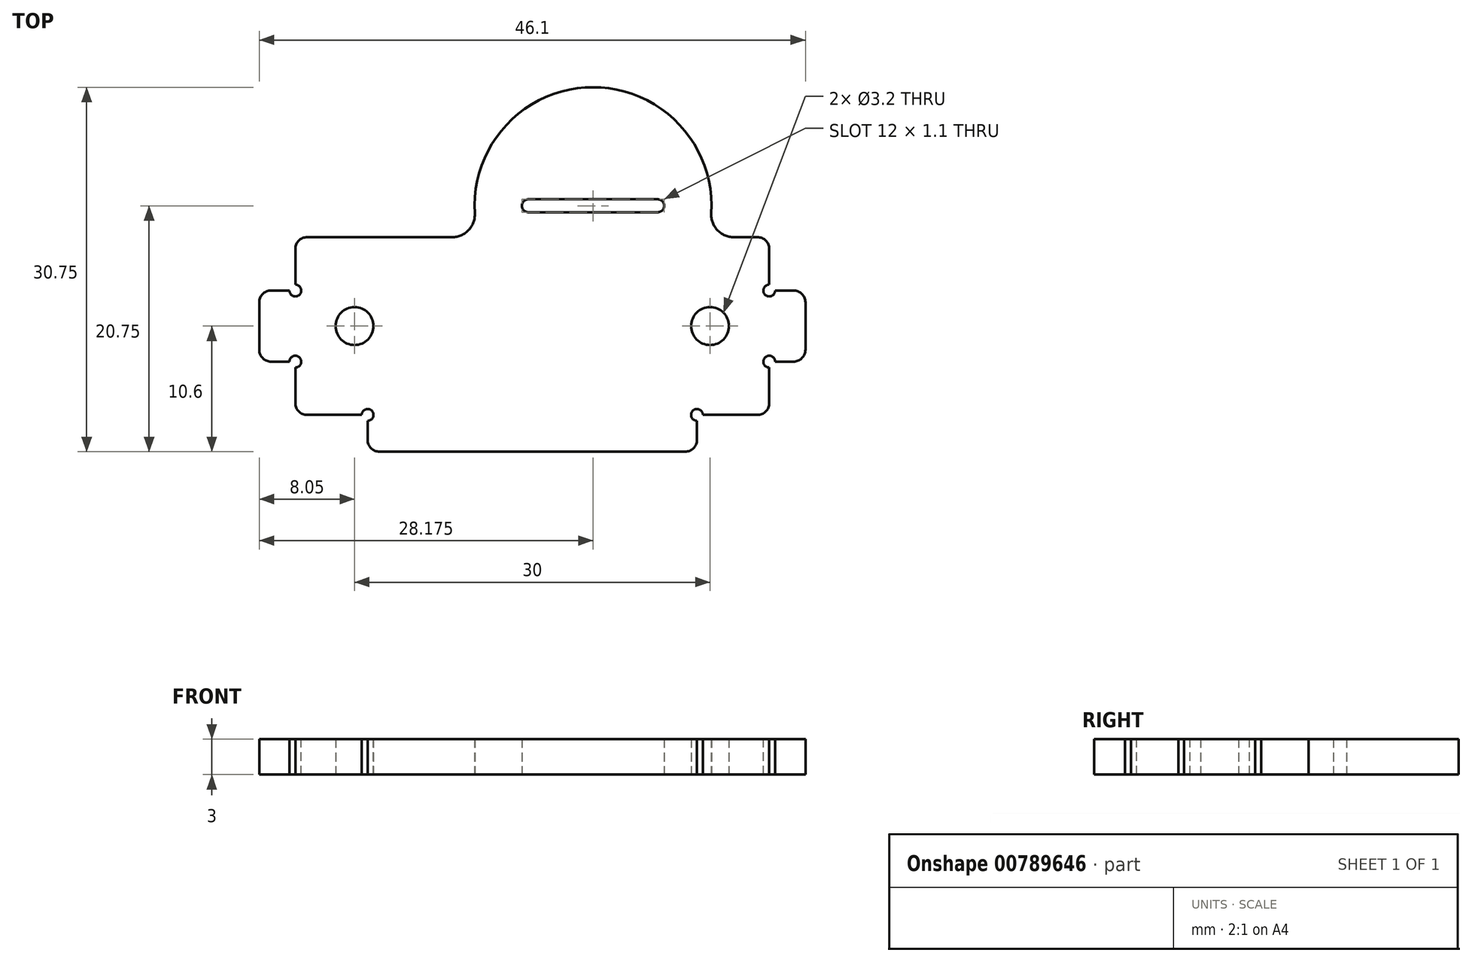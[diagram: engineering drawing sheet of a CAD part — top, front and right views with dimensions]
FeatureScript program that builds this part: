
annotation { "Feature Type Name" : "Feature", "Feature Type Description" : "" }
export const myFeature = defineFeature(function(context is Context, id is Id, definition is map)
    precondition{}
    {
        {
            var Q0;
            Q0=qCreatedBy(makeId("Top.planeOp"),FACE);
            var sketch = newSketch(context, id + "F0", { "sketchPlane" : qUnion([Q0])});
            skLineSegment(sketch, "E0", {"start": v(0, 0) * mm, "end": v(-20, 0) * mm, "construction": true});
            skLineSegment(sketch, "E1", {"start": v(0, 0) * mm, "end": v(0, 11.6) * mm, "construction": true});
            skLineSegment(sketch, "E2.MirrorCS", {"start": v(-20, -7.5) * mm, "end": v(-13.9, -7.5) * mm});
            skLineSegment(sketch, "E3.MirrorCS", {"start": v(-13.9, -10.6) * mm, "end": v(-13.9, -7.5) * mm});
            skLineSegment(sketch, "E4.MirrorCS", {"start": v(20, 7.5) * mm, "end": v(17, 7.5) * mm});
            skLineSegment(sketch, "E5.MirrorCS", {"start": v(20, -7.5) * mm, "end": v(13.9, -7.5) * mm});
            skLineSegment(sketch, "E6.MirrorCS", {"start": v(13.9, -10.6) * mm, "end": v(13.9, -7.5) * mm});
            skCircle(sketch, "E7", {"center": v(-15, 0) * mm, "radius": 1.6 * mm});
            skCircle(sketch, "E8.MirrorC", {"center": v(15, 0) * mm, "radius": 1.6 * mm});
            skCircle(sketch, "E9", {"center": v(5.13, 10.15) * mm, "radius": 6 * mm, "construction": true});
            skPoint(sketch, "E10.visualSharp", {"position": v(4.24, 7.5) * mm});
            skLineSegment(sketch, "E11", {"start": v(-20, 7.5) * mm, "end": v(-6.75, 7.5) * mm});
            skArc(sketch, "E12", {"start": v(15.1, 9.52) * mm, "mid": v(5.13, 20.15) * mm, "end": v(-4.86, 9.52) * mm});
            skPoint(sketch, "E13.visualSharp", {"position": v(-1.05, 7.5) * mm});
            skArc(sketch, "E13.filletArc", {"start": v(-6.75, 7.5) * mm, "mid": v(-5.37, 8.1) * mm, "end": v(-4.86, 9.52) * mm});
            skPoint(sketch, "E14.visualSharp", {"position": v(13.56, 7.5) * mm});
            skArc(sketch, "E14.filletArc", {"start": v(15.1, 9.52) * mm, "mid": v(15.62, 8.1) * mm, "end": v(17, 7.5) * mm});
            skLineSegment(sketch, "E15", {"start": v(-4.86, 9.52) * mm, "end": v(15.1, 9.52) * mm, "construction": true});
            skLineSegment(sketch, "E16.trimOffspring", {"start": v(-20, 7.5) * mm, "end": v(-20, 0) * mm});
            skLineSegment(sketch, "E17.trimOffspring", {"start": v(-20, -7.5) * mm, "end": v(-20, 0) * mm});
            skLineSegment(sketch, "E18.trimOffspring", {"start": v(20, -7.5) * mm, "end": v(20, 0) * mm});
            skLineSegment(sketch, "E19.trimOffspring", {"start": v(20, 7.5) * mm, "end": v(20, 0) * mm});
            skCircle(sketch, "E20", {"center": v(15, 0) * mm, "radius": 3 * mm, "construction": true});
            skCircle(sketch, "E21", {"center": v(-15, 0) * mm, "radius": 3 * mm, "construction": true});
            skLineSegment(sketch, "E22", {"start": v(-13.9, -10.6) * mm, "end": v(13.9, -10.6) * mm});
            skLineSegment(sketch, "E23.bottom", {"start": v(-0.32, 10.7) * mm, "end": v(10.58, 10.7) * mm});
            skLineSegment(sketch, "E23.top", {"start": v(-0.32, 9.6) * mm, "end": v(10.58, 9.6) * mm});
            skLineSegment(sketch, "E23.left", {"start": v(-0.32, 10.7) * mm, "end": v(-0.32, 9.6) * mm, "construction": true});
            skLineSegment(sketch, "E23.right", {"start": v(10.58, 10.7) * mm, "end": v(10.58, 9.6) * mm, "construction": true});
            skLineSegment(sketch, "E24", {"start": v(-0.32, 10.15) * mm, "end": v(10.58, 10.15) * mm, "construction": true});
            skCircle(sketch, "E25", {"center": v(-0.32, 10.15) * mm, "radius": 0.55 * mm});
            skCircle(sketch, "E26", {"center": v(10.58, 10.15) * mm, "radius": 0.55 * mm});
            skSolve(sketch);
        }
        {
            var Q0;
            Q0 = qSketchRegion(id + "F0", true);
            extrude(context, id + "F1", {"entities" : qUnion([Q0]), "depth" : 3 * mm, "offsetDistance" : 25 * mm});
        }
        {
            var Q0;
            Q0=makeQuery(id+"F1.opExtrude","CAP_FACE",FACE,{"disambiguationData":[OSD([sQuery(id+"F0.wireOp",EDGE,"E2.MirrorCS"),sQuery(id+"F0.wireOp",EDGE,"E3.MirrorCS"),sQuery(id+"F0.wireOp",EDGE,"E4.MirrorCS"),sQuery(id+"F0.wireOp",EDGE,"E5.MirrorCS"),sQuery(id+"F0.wireOp",EDGE,"E6.MirrorCS"),sQuery(id+"F0.wireOp",EDGE,"E7"),sQuery(id+"F0.wireOp",EDGE,"E8.MirrorC"),sQuery(id+"F0.wireOp",EDGE,"E9"),sQuery(id+"F0.wireOp",EDGE,"E11"),sQuery(id+"F0.wireOp",EDGE,"E12"),sQuery(id+"F0.wireOp",EDGE,"E13.filletArc"),sQuery(id+"F0.wireOp",EDGE,"E14.filletArc"),sQuery(id+"F0.wireOp",EDGE,"E16.trimOffspring"),sQuery(id+"F0.wireOp",EDGE,"E17.trimOffspring"),sQuery(id+"F0.wireOp",EDGE,"E18.trimOffspring"),sQuery(id+"F0.wireOp",EDGE,"E19.trimOffspring"),sQuery(id+"F0.wireOp",EDGE,"E22")])],"isStart":false});
            var sketch = newSketch(context, id + "F2", { "sketchPlane" : qUnion([Q0])});
            skLineSegment(sketch, "E27.bottom", {"start": v(-20, -3) * mm, "end": v(-23.05, -3) * mm});
            skLineSegment(sketch, "E27.top", {"start": v(-20, 3) * mm, "end": v(-23.05, 3) * mm});
            skLineSegment(sketch, "E27.left", {"start": v(-20, -3) * mm, "end": v(-20, 3) * mm});
            skLineSegment(sketch, "E27.right", {"start": v(-23.05, -3) * mm, "end": v(-23.05, 3) * mm});
            skLineSegment(sketch, "E28.MirrorCS", {"start": v(20, 3) * mm, "end": v(23.05, 3) * mm});
            skLineSegment(sketch, "E29.MirrorCS", {"start": v(20, -3) * mm, "end": v(20, 3) * mm});
            skLineSegment(sketch, "E30.MirrorCS", {"start": v(20, -3) * mm, "end": v(23.05, -3) * mm});
            skLineSegment(sketch, "E31.MirrorCS", {"start": v(23.05, -3) * mm, "end": v(23.05, 3) * mm});
            skSolve(sketch);
        }
        {
            var Q0;
            Q0 = qSketchRegion(id + "F2", true);
            var Q1;
            Q1=makeQuery(id+"F1.opExtrude","CAP_FACE",FACE,{"disambiguationData":[OSD([sQuery(id+"F0.wireOp",EDGE,"E2.MirrorCS"),sQuery(id+"F0.wireOp",EDGE,"E3.MirrorCS"),sQuery(id+"F0.wireOp",EDGE,"E4.MirrorCS"),sQuery(id+"F0.wireOp",EDGE,"E5.MirrorCS"),sQuery(id+"F0.wireOp",EDGE,"E6.MirrorCS"),sQuery(id+"F0.wireOp",EDGE,"E7"),sQuery(id+"F0.wireOp",EDGE,"E8.MirrorC"),sQuery(id+"F0.wireOp",EDGE,"E9"),sQuery(id+"F0.wireOp",EDGE,"E11"),sQuery(id+"F0.wireOp",EDGE,"E12"),sQuery(id+"F0.wireOp",EDGE,"E13.filletArc"),sQuery(id+"F0.wireOp",EDGE,"E14.filletArc"),sQuery(id+"F0.wireOp",EDGE,"E16.trimOffspring"),sQuery(id+"F0.wireOp",EDGE,"E17.trimOffspring"),sQuery(id+"F0.wireOp",EDGE,"E18.trimOffspring"),sQuery(id+"F0.wireOp",EDGE,"E19.trimOffspring"),sQuery(id+"F0.wireOp",EDGE,"E22")])],"isStart":true});
            extrude(context, id + "F3", {"entities" : qUnion([Q0]), "operationType" : NewBodyOperationType.ADD, "endBound" : BoundingType.UP_TO_SURFACE, "oppositeDirection" : true, "depth" : 25 * mm, "endBoundEntityFace" : qUnion([Q1]), "offsetDistance" : 25 * mm});
        }
        {
            var Q0;
            Q0=makeQuery(id+"F3.boolean.opBoolean","MERGE",FACE,{"derivedFrom":[makeQuery(id+"F1.opExtrude","CAP_FACE",FACE,{"disambiguationData":[OSD([sQuery(id+"F0.wireOp",EDGE,"E2.MirrorCS"),sQuery(id+"F0.wireOp",EDGE,"E3.MirrorCS"),sQuery(id+"F0.wireOp",EDGE,"E4.MirrorCS"),sQuery(id+"F0.wireOp",EDGE,"E5.MirrorCS"),sQuery(id+"F0.wireOp",EDGE,"E6.MirrorCS"),sQuery(id+"F0.wireOp",EDGE,"E7"),sQuery(id+"F0.wireOp",EDGE,"E8.MirrorC"),sQuery(id+"F0.wireOp",EDGE,"E9"),sQuery(id+"F0.wireOp",EDGE,"E11"),sQuery(id+"F0.wireOp",EDGE,"E12"),sQuery(id+"F0.wireOp",EDGE,"E13.filletArc"),sQuery(id+"F0.wireOp",EDGE,"E14.filletArc"),sQuery(id+"F0.wireOp",EDGE,"E16.trimOffspring"),sQuery(id+"F0.wireOp",EDGE,"E17.trimOffspring"),sQuery(id+"F0.wireOp",EDGE,"E18.trimOffspring"),sQuery(id+"F0.wireOp",EDGE,"E19.trimOffspring"),sQuery(id+"F0.wireOp",EDGE,"E22")])],"isStart":false}),makeQuery(id+"F3.opExtrude","CAP_FACE",FACE,{"disambiguationData":[OSD([sQuery(id+"F2.wireOp",EDGE,"E27.bottom"),sQuery(id+"F2.wireOp",EDGE,"E27.top"),sQuery(id+"F2.wireOp",EDGE,"E27.left"),sQuery(id+"F2.wireOp",EDGE,"E27.right")])],"isStart":true}),makeQuery(id+"F3.opExtrude","CAP_FACE",FACE,{"disambiguationData":[OSD([sQuery(id+"F2.wireOp",EDGE,"E28.MirrorCS"),sQuery(id+"F2.wireOp",EDGE,"E29.MirrorCS"),sQuery(id+"F2.wireOp",EDGE,"E30.MirrorCS"),sQuery(id+"F2.wireOp",EDGE,"E31.MirrorCS")])],"isStart":true})]});
            var sketch = newSketch(context, id + "F4", { "sketchPlane" : qUnion([Q0])});
            skPoint(sketch, "E32", {"position": v(13.9, -7.5) * mm});
            skPoint(sketch, "E33", {"position": v(20, -3) * mm});
            skPoint(sketch, "E34", {"position": v(20, 3) * mm});
            skPoint(sketch, "E35", {"position": v(-13.9, -7.5) * mm});
            skPoint(sketch, "E36", {"position": v(-20, -3) * mm});
            skPoint(sketch, "E37", {"position": v(-20, 3) * mm});
            skSolve(sketch);
        }
        {
            var Q0;
            Q0=sQuery(id+"F4.wireOp",VERTEX,"E32");
            var Q1;
            Q1=sQuery(id+"F4.wireOp",VERTEX,"E33");
            var Q2;
            Q2=sQuery(id+"F4.wireOp",VERTEX,"E34");
            var Q3;
            Q3=sQuery(id+"F4.wireOp",VERTEX,"E35");
            var Q4;
            Q4=sQuery(id+"F4.wireOp",VERTEX,"E36");
            var Q5;
            Q5=sQuery(id+"F4.wireOp",VERTEX,"E37");
            var Q6;
            Q6=makeQuery(id+"F1.opExtrude","SWEPT_BODY",BODY,{"disambiguationData":[OSD([sQuery(id+"F0.wireOp",EDGE,"E2.MirrorCS"),sQuery(id+"F0.wireOp",EDGE,"E3.MirrorCS"),sQuery(id+"F0.wireOp",EDGE,"E4.MirrorCS"),sQuery(id+"F0.wireOp",EDGE,"E5.MirrorCS"),sQuery(id+"F0.wireOp",EDGE,"E6.MirrorCS"),sQuery(id+"F0.wireOp",EDGE,"E7"),sQuery(id+"F0.wireOp",EDGE,"E8.MirrorC"),sQuery(id+"F0.wireOp",EDGE,"E9"),sQuery(id+"F0.wireOp",EDGE,"E11"),sQuery(id+"F0.wireOp",EDGE,"E12"),sQuery(id+"F0.wireOp",EDGE,"E13.filletArc"),sQuery(id+"F0.wireOp",EDGE,"E14.filletArc"),sQuery(id+"F0.wireOp",EDGE,"E16.trimOffspring"),sQuery(id+"F0.wireOp",EDGE,"E17.trimOffspring"),sQuery(id+"F0.wireOp",EDGE,"E18.trimOffspring"),sQuery(id+"F0.wireOp",EDGE,"E19.trimOffspring"),sQuery(id+"F0.wireOp",EDGE,"E22")])]});
            hole(context, id + "F5", {"style" : HoleStyle.SIMPLE, "endStyle" : HoleEndStyle.THROUGH, "holeDiameter" : 1 * mm, "majorDiameter" : 5 * mm, "isTappedThrough" : true, "tappedDepth" : 12 * mm, "tapClearance" : 3, "locations" : qUnion([Q0, Q1, Q2, Q3, Q4, Q5]), "scope" : qUnion([Q6])});
        }
        {
            var Q0;
            Q0=makeQuery(id+"F1.opExtrude","SWEPT_EDGE",EDGE,{"disambiguationData":[OSD([sQuery(id+"F0.wireOp",EDGE,"E4.MirrorCS"),sQuery(id+"F0.wireOp",EDGE,"E19.trimOffspring")])]});
            var Q1;
            {var subQ1=sQuery(id+"F0.wireOp",EDGE,"E19.trimOffspring");var subQ2=sQuery(id+"F0.wireOp",EDGE,"E18.trimOffspring");var subQ14=sQuery(id+"F0.wireOp",EDGE,"E4.MirrorCS");Q1=makeQuery(id+"F5.hole-2.boolean.opBoolean","INTERSECT",EDGE,{"derivedFrom":[makeQuery(id+"F3.boolean.opBoolean","SPLIT",FACE,{"disambiguationData":[TD([makeQuery(id+"F1.opExtrude","SWEPT_FACE",FACE,{"disambiguationData":[OSD([subQ14])]})])],"derivedFrom":makeQuery(id+"F1.opExtrude","SWEPT_FACE",FACE,{"disambiguationData":[OSD([subQ2,subQ1])]})}),makeQuery(id+"F5.hole-2.opRevolve","SWEPT_FACE",FACE,{"disambiguationData":[OSD([sQuery(id+"F5.hole-2.sketch.wireOp",EDGE,"core_line_2")])]})]});}
            var Q2;
            Q2=makeQuery(id+"F5.hole-2.boolean.opBoolean","INTERSECT",EDGE,{"derivedFrom":[makeQuery(id+"F3.opExtrude","SWEPT_FACE",FACE,{"disambiguationData":[OSD([sQuery(id+"F2.wireOp",EDGE,"E28.MirrorCS")])]}),makeQuery(id+"F5.hole-2.opRevolve","SWEPT_FACE",FACE,{"disambiguationData":[OSD([sQuery(id+"F5.hole-2.sketch.wireOp",EDGE,"core_line_2")])]})]});
            var Q3;
            Q3=makeQuery(id+"F3.opExtrude","SWEPT_EDGE",EDGE,{"disambiguationData":[OSD([sQuery(id+"F2.wireOp",EDGE,"E28.MirrorCS"),sQuery(id+"F2.wireOp",EDGE,"E31.MirrorCS")])]});
            var Q4;
            Q4=makeQuery(id+"F3.opExtrude","SWEPT_EDGE",EDGE,{"disambiguationData":[OSD([sQuery(id+"F2.wireOp",EDGE,"E30.MirrorCS"),sQuery(id+"F2.wireOp",EDGE,"E31.MirrorCS")])]});
            var Q5;
            {var subQ1=sQuery(id+"F0.wireOp",EDGE,"E19.trimOffspring");var subQ2=sQuery(id+"F0.wireOp",EDGE,"E18.trimOffspring");var subQ13=sQuery(id+"F0.wireOp",EDGE,"E5.MirrorCS");Q5=makeQuery(id+"F5.hole-1.boolean.opBoolean","INTERSECT",EDGE,{"derivedFrom":[makeQuery(id+"F3.boolean.opBoolean","SPLIT",FACE,{"disambiguationData":[TD([makeQuery(id+"F1.opExtrude","SWEPT_FACE",FACE,{"disambiguationData":[OSD([subQ13])]})])],"derivedFrom":makeQuery(id+"F1.opExtrude","SWEPT_FACE",FACE,{"disambiguationData":[OSD([subQ2,subQ1])]})}),makeQuery(id+"F5.hole-1.opRevolve","SWEPT_FACE",FACE,{"disambiguationData":[OSD([sQuery(id+"F5.hole-1.sketch.wireOp",EDGE,"core_line_2")])]})]});}
            var Q6;
            Q6=makeQuery(id+"F5.hole-0.boolean.opBoolean","INTERSECT",EDGE,{"derivedFrom":[makeQuery(id+"F1.opExtrude","SWEPT_FACE",FACE,{"disambiguationData":[OSD([sQuery(id+"F0.wireOp",EDGE,"E6.MirrorCS")])]}),makeQuery(id+"F5.hole-0.opRevolve","SWEPT_FACE",FACE,{"disambiguationData":[OSD([sQuery(id+"F5.hole-0.sketch.wireOp",EDGE,"core_line_2")])]})]});
            var Q7;
            Q7=makeQuery(id+"F1.opExtrude","SWEPT_EDGE",EDGE,{"disambiguationData":[OSD([sQuery(id+"F0.wireOp",EDGE,"E6.MirrorCS"),sQuery(id+"F0.wireOp",EDGE,"E22")])]});
            var Q8;
            Q8=makeQuery(id+"F1.opExtrude","SWEPT_EDGE",EDGE,{"disambiguationData":[OSD([sQuery(id+"F0.wireOp",EDGE,"E5.MirrorCS"),sQuery(id+"F0.wireOp",EDGE,"E18.trimOffspring")])]});
            var Q9;
            Q9=makeQuery(id+"F5.hole-3.boolean.opBoolean","INTERSECT",EDGE,{"derivedFrom":[makeQuery(id+"F1.opExtrude","SWEPT_FACE",FACE,{"disambiguationData":[OSD([sQuery(id+"F0.wireOp",EDGE,"E3.MirrorCS")])]}),makeQuery(id+"F5.hole-3.opRevolve","SWEPT_FACE",FACE,{"disambiguationData":[OSD([sQuery(id+"F5.hole-3.sketch.wireOp",EDGE,"core_line_2")])]})]});
            var Q10;
            Q10=makeQuery(id+"F5.hole-3.boolean.opBoolean","INTERSECT",EDGE,{"derivedFrom":[makeQuery(id+"F1.opExtrude","SWEPT_FACE",FACE,{"disambiguationData":[OSD([sQuery(id+"F0.wireOp",EDGE,"E2.MirrorCS")])]}),makeQuery(id+"F5.hole-3.opRevolve","SWEPT_FACE",FACE,{"disambiguationData":[OSD([sQuery(id+"F5.hole-3.sketch.wireOp",EDGE,"core_line_2")])]})]});
            var Q11;
            {var subQ4=sQuery(id+"F0.wireOp",EDGE,"E17.trimOffspring");var subQ5=sQuery(id+"F0.wireOp",EDGE,"E16.trimOffspring");var subQ17=sQuery(id+"F0.wireOp",EDGE,"E2.MirrorCS");Q11=makeQuery(id+"F5.hole-4.boolean.opBoolean","INTERSECT",EDGE,{"derivedFrom":[makeQuery(id+"F3.boolean.opBoolean","SPLIT",FACE,{"disambiguationData":[TD([makeQuery(id+"F1.opExtrude","SWEPT_FACE",FACE,{"disambiguationData":[OSD([subQ17])]})])],"derivedFrom":makeQuery(id+"F1.opExtrude","SWEPT_FACE",FACE,{"disambiguationData":[OSD([subQ5,subQ4])]})}),makeQuery(id+"F5.hole-4.opRevolve","SWEPT_FACE",FACE,{"disambiguationData":[OSD([sQuery(id+"F5.hole-4.sketch.wireOp",EDGE,"core_line_2")])]})]});}
            var Q12;
            Q12=makeQuery(id+"F5.hole-4.boolean.opBoolean","INTERSECT",EDGE,{"derivedFrom":[makeQuery(id+"F3.opExtrude","SWEPT_FACE",FACE,{"disambiguationData":[OSD([sQuery(id+"F2.wireOp",EDGE,"E27.bottom")])]}),makeQuery(id+"F5.hole-4.opRevolve","SWEPT_FACE",FACE,{"disambiguationData":[OSD([sQuery(id+"F5.hole-4.sketch.wireOp",EDGE,"core_line_2")])]})]});
            var Q13;
            Q13=makeQuery(id+"F5.hole-5.boolean.opBoolean","INTERSECT",EDGE,{"derivedFrom":[makeQuery(id+"F3.opExtrude","SWEPT_FACE",FACE,{"disambiguationData":[OSD([sQuery(id+"F2.wireOp",EDGE,"E27.top")])]}),makeQuery(id+"F5.hole-5.opRevolve","SWEPT_FACE",FACE,{"disambiguationData":[OSD([sQuery(id+"F5.hole-5.sketch.wireOp",EDGE,"core_line_2")])]})]});
            var Q14;
            Q14=makeQuery(id+"F3.opExtrude","SWEPT_EDGE",EDGE,{"disambiguationData":[OSD([sQuery(id+"F2.wireOp",EDGE,"E27.top"),sQuery(id+"F2.wireOp",EDGE,"E27.right")])]});
            var Q15;
            Q15=makeQuery(id+"F1.opExtrude","SWEPT_EDGE",EDGE,{"disambiguationData":[OSD([sQuery(id+"F0.wireOp",EDGE,"E11"),sQuery(id+"F0.wireOp",EDGE,"E16.trimOffspring")])]});
            var Q16;
            {var subQ4=sQuery(id+"F0.wireOp",EDGE,"E17.trimOffspring");var subQ5=sQuery(id+"F0.wireOp",EDGE,"E16.trimOffspring");var subQ9=sQuery(id+"F0.wireOp",EDGE,"E11");Q16=makeQuery(id+"F5.hole-5.boolean.opBoolean","INTERSECT",EDGE,{"derivedFrom":[makeQuery(id+"F3.boolean.opBoolean","SPLIT",FACE,{"disambiguationData":[TD([makeQuery(id+"F1.opExtrude","SWEPT_FACE",FACE,{"disambiguationData":[OSD([subQ9])]})])],"derivedFrom":makeQuery(id+"F1.opExtrude","SWEPT_FACE",FACE,{"disambiguationData":[OSD([subQ5,subQ4])]})}),makeQuery(id+"F5.hole-5.opRevolve","SWEPT_FACE",FACE,{"disambiguationData":[OSD([sQuery(id+"F5.hole-5.sketch.wireOp",EDGE,"core_line_2")])]})]});}
            var Q17;
            Q17=makeQuery(id+"F1.opExtrude","SWEPT_EDGE",EDGE,{"disambiguationData":[OSD([sQuery(id+"F0.wireOp",EDGE,"E2.MirrorCS"),sQuery(id+"F0.wireOp",EDGE,"E17.trimOffspring")])]});
            var Q18;
            Q18=makeQuery(id+"F1.opExtrude","SWEPT_EDGE",EDGE,{"disambiguationData":[OSD([sQuery(id+"F0.wireOp",EDGE,"E3.MirrorCS"),sQuery(id+"F0.wireOp",EDGE,"E22")])]});
            var Q19;
            Q19=makeQuery(id+"F5.hole-0.boolean.opBoolean","INTERSECT",EDGE,{"derivedFrom":[makeQuery(id+"F1.opExtrude","SWEPT_FACE",FACE,{"disambiguationData":[OSD([sQuery(id+"F0.wireOp",EDGE,"E5.MirrorCS")])]}),makeQuery(id+"F5.hole-0.opRevolve","SWEPT_FACE",FACE,{"disambiguationData":[OSD([sQuery(id+"F5.hole-0.sketch.wireOp",EDGE,"core_line_2")])]})]});
            var Q20;
            Q20=makeQuery(id+"F5.hole-1.boolean.opBoolean","INTERSECT",EDGE,{"derivedFrom":[makeQuery(id+"F3.opExtrude","SWEPT_FACE",FACE,{"disambiguationData":[OSD([sQuery(id+"F2.wireOp",EDGE,"E30.MirrorCS")])]}),makeQuery(id+"F5.hole-1.opRevolve","SWEPT_FACE",FACE,{"disambiguationData":[OSD([sQuery(id+"F5.hole-1.sketch.wireOp",EDGE,"core_line_2")])]})]});
            var Q21;
            Q21=makeQuery(id+"F3.opExtrude","SWEPT_EDGE",EDGE,{"disambiguationData":[OSD([sQuery(id+"F2.wireOp",EDGE,"E27.bottom"),sQuery(id+"F2.wireOp",EDGE,"E27.right")])]});
            fillet(context, id + "F6", {"entities" : qUnion([Q0, Q1, Q2, Q3, Q4, Q5, Q6, Q7, Q8, Q9, Q10, Q11, Q12, Q13, Q14, Q15, Q16, Q17, Q18, Q19, Q20, Q21]), "radius" : 1 * mm, "tangentPropagation" : true, "allowEdgeOverflow" : false});
        }
    });
